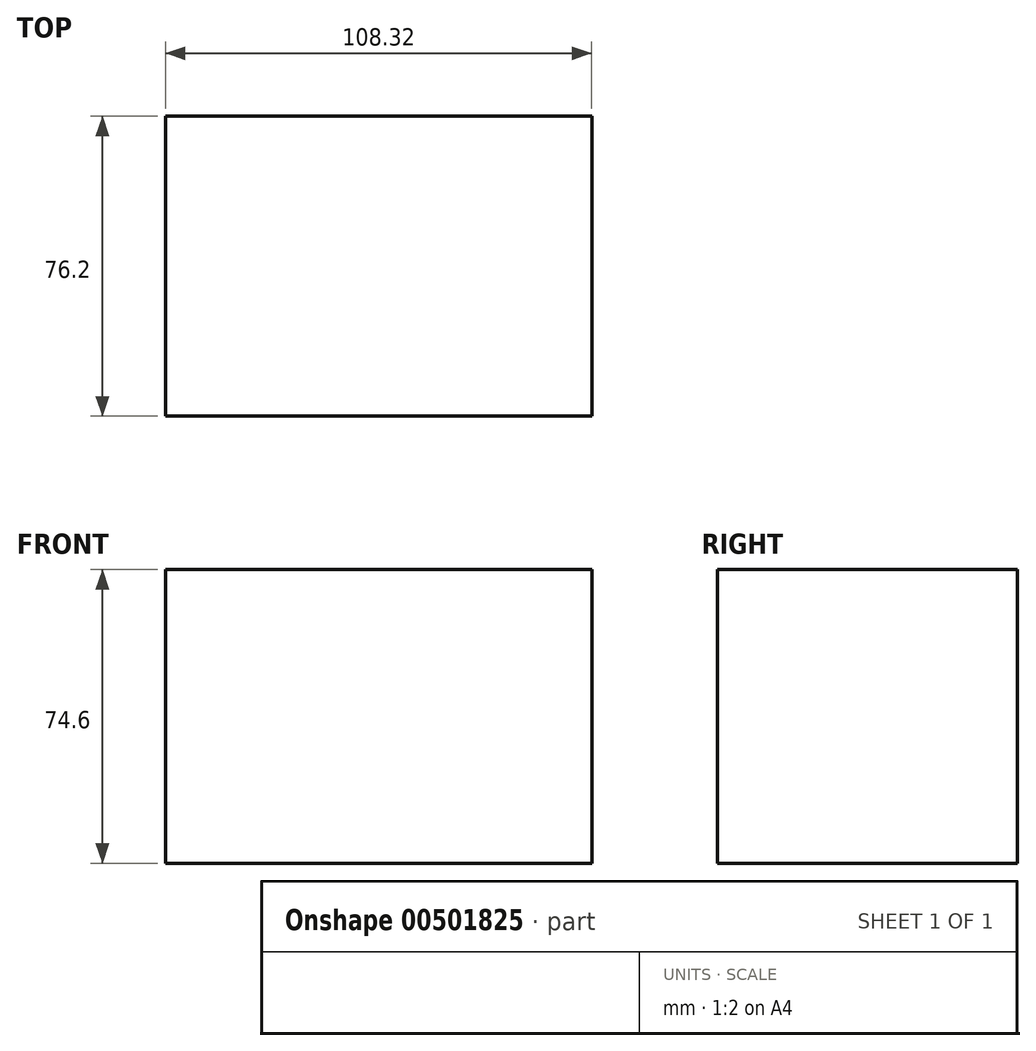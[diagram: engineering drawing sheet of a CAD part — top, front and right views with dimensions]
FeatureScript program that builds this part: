
annotation { "Feature Type Name" : "Feature", "Feature Type Description" : "" }
export const myFeature = defineFeature(function(context is Context, id is Id, definition is map)
    precondition{}
    {
        {
            var Q0;
            Q0=qCreatedBy(makeId("Front.planeOp"),FACE);
            var sketch = newSketch(context, id + "F0", { "sketchPlane" : qUnion([Q0])});
            skLineSegment(sketch, "E0.bottom", {"start": v(0, 99.12) * mm, "end": v(108.32, 99.12) * mm});
            skLineSegment(sketch, "E0.top", {"start": v(0, 24.52) * mm, "end": v(108.32, 24.52) * mm});
            skLineSegment(sketch, "E0.left", {"start": v(0, 99.12) * mm, "end": v(0, 24.52) * mm});
            skLineSegment(sketch, "E0.right", {"start": v(108.32, 99.12) * mm, "end": v(108.32, 24.52) * mm});
            skLineSegment(sketch, "E1.bottom", {"start": v(74.72, 99.12) * mm, "end": v(54.16, 99.12) * mm});
            skLineSegment(sketch, "E1.top", {"start": v(74.72, 99.12) * mm, "end": v(54.16, 99.12) * mm});
            skLineSegment(sketch, "E1.left", {"start": v(74.72, 99.12) * mm, "end": v(74.72, 99.12) * mm});
            skLineSegment(sketch, "E1.right", {"start": v(54.16, 99.12) * mm, "end": v(54.16, 99.12) * mm});
            skSolve(sketch);
        }
        {
            var Q0;
            Q0 = qSketchRegion(id + "F0", true);
            extrude(context, id + "F1", {"entities" : qUnion([Q0]), "depth" : 76.2 * mm});
        }
    });
